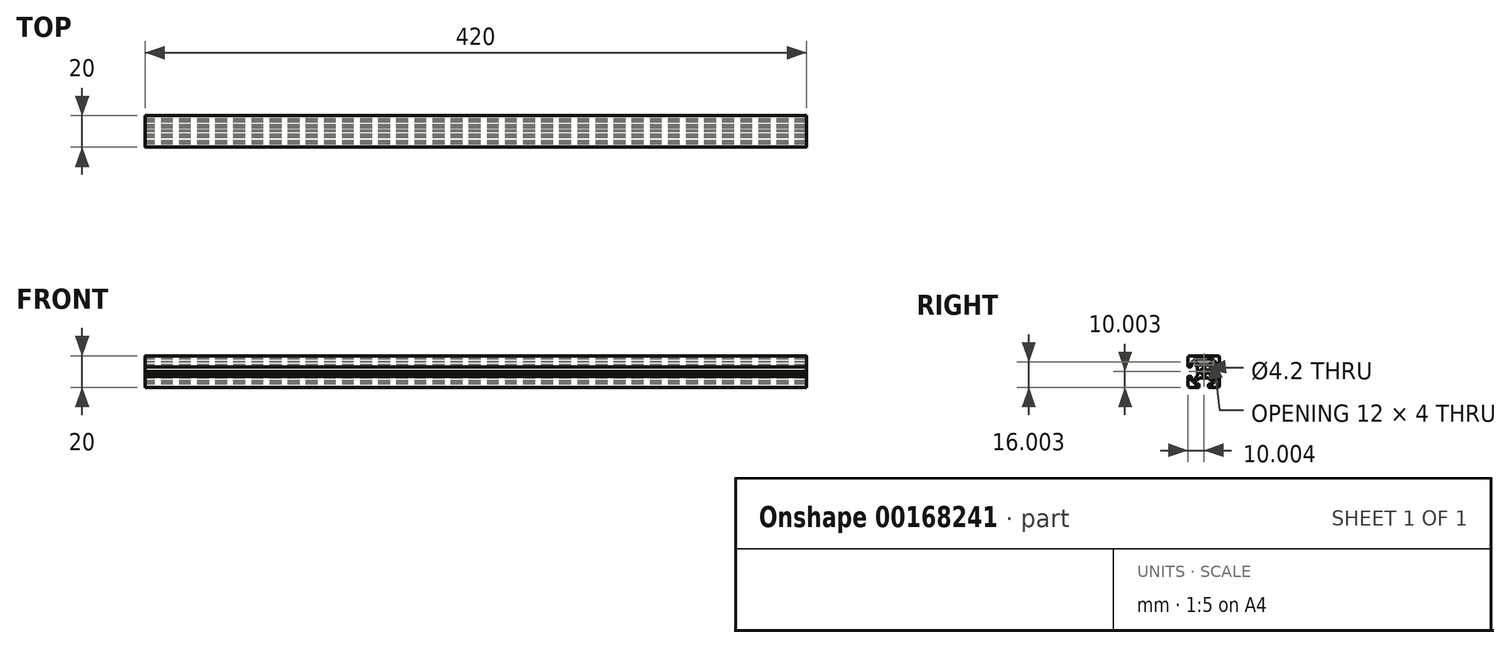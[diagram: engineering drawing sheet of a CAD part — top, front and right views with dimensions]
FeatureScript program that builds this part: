
annotation { "Feature Type Name" : "Feature", "Feature Type Description" : "" }
export const myFeature = defineFeature(function(context is Context, id is Id, definition is map)
    precondition{}
    {
        {
            var Q0;
            Q0=qCreatedBy(makeId("Right.planeOp"),FACE);
            var sketch = newSketch(context, id + "F0", { "sketchPlane" : qUnion([Q0])});
            skLineSegment(sketch, "E0", {"start": v(0.04, 10.07) * mm, "end": v(-8.96, 10.07) * mm});
            skLineSegment(sketch, "E1", {"start": v(-9.96, 9.07) * mm, "end": v(-9.96, 3.37) * mm});
            skLineSegment(sketch, "E2", {"start": v(-3.96, 3.01) * mm, "end": v(-3.96, 0.73) * mm});
            skLineSegment(sketch, "E3", {"start": v(0.04, 4.07) * mm, "end": v(-2.69, 4.07) * mm});
            skLineSegment(sketch, "E4", {"start": v(0.04, 8.07) * mm, "end": v(-5.46, 8.07) * mm});
            skLineSegment(sketch, "E5", {"start": v(-7.96, 6.07) * mm, "end": v(-7.96, 3.37) * mm});
            skLineSegment(sketch, "E6", {"start": v(-8.26, 3.07) * mm, "end": v(-9.66, 3.07) * mm});
            skLineSegment(sketch, "E7", {"start": v(-8.26, -2.93) * mm, "end": v(-9.66, -2.93) * mm});
            skLineSegment(sketch, "E8", {"start": v(-7.02, -5.93) * mm, "end": v(-7.96, -5.93) * mm});
            skLineSegment(sketch, "E9", {"start": v(-7.96, -3.23) * mm, "end": v(-7.96, -5.93) * mm});
            skLineSegment(sketch, "E10", {"start": v(-9.96, -3.23) * mm, "end": v(-9.96, -8.93) * mm});
            skLineSegment(sketch, "E11", {"start": v(-7.02, 6.07) * mm, "end": v(-7.96, 6.07) * mm});
            skLineSegment(sketch, "E12", {"start": v(-3.89, -0.33) * mm, "end": v(-3.66, 0.07) * mm});
            skLineSegment(sketch, "E13", {"start": v(-3.89, 0.48) * mm, "end": v(-3.66, 0.07) * mm});
            skLineSegment(sketch, "E14", {"start": v(-3.96, -2.43) * mm, "end": v(-3.96, -2.87) * mm});
            skLineSegment(sketch, "E15", {"start": v(-3.96, 3.01) * mm, "end": v(-7.02, 6.07) * mm});
            skLineSegment(sketch, "E16", {"start": v(-3.96, -2.87) * mm, "end": v(-7.02, -5.93) * mm});
            skLineSegment(sketch, "E17", {"start": v(-3.96, -2.43) * mm, "end": v(-3.7, -1.15) * mm});
            skArc(sketch, "E18", {"start": v(-3.89, -0.33) * mm, "mid": v(-3.96, -0.58) * mm, "end": v(-3.89, -0.83) * mm});
            skLineSegment(sketch, "E19", {"start": v(-3.89, -0.83) * mm, "end": v(-3.7, -1.15) * mm});
            skArc(sketch, "E20", {"start": v(-3.96, 0.73) * mm, "mid": v(-3.94, 0.6) * mm, "end": v(-3.89, 0.48) * mm});
            skArc(sketch, "E21", {"start": v(-8.26, 3.07) * mm, "mid": v(-8.04, 3.16) * mm, "end": v(-7.96, 3.37) * mm});
            skArc(sketch, "E22", {"start": v(-9.96, 3.37) * mm, "mid": v(-9.87, 3.16) * mm, "end": v(-9.66, 3.07) * mm});
            skArc(sketch, "E23", {"start": v(-7.96, -3.23) * mm, "mid": v(-8.04, -3.01) * mm, "end": v(-8.26, -2.93) * mm});
            skArc(sketch, "E24", {"start": v(-9.66, -2.93) * mm, "mid": v(-9.87, -3.01) * mm, "end": v(-9.96, -3.23) * mm});
            skLineSegment(sketch, "E25", {"start": v(-2.9, -3.93) * mm, "end": v(-0.61, -3.93) * mm});
            skArc(sketch, "E26", {"start": v(-3.26, -9.93) * mm, "mid": v(-3.04, -9.84) * mm, "end": v(-2.96, -9.63) * mm});
            skLineSegment(sketch, "E27", {"start": v(-5.96, -7.93) * mm, "end": v(-3.26, -7.93) * mm});
            skArc(sketch, "E28", {"start": v(-2.96, -8.23) * mm, "mid": v(-3.04, -8.01) * mm, "end": v(-3.26, -7.93) * mm});
            skLineSegment(sketch, "E29", {"start": v(-5.96, -6.99) * mm, "end": v(-5.96, -7.93) * mm});
            skLineSegment(sketch, "E30", {"start": v(-2.96, -8.23) * mm, "end": v(-2.96, -9.63) * mm});
            skLineSegment(sketch, "E31", {"start": v(-0.36, -3.86) * mm, "end": v(-0.06, -3.69) * mm});
            skArc(sketch, "E32", {"start": v(-0.61, -3.93) * mm, "mid": v(-0.48, -3.9) * mm, "end": v(-0.36, -3.86) * mm});
            skLineSegment(sketch, "E33", {"start": v(-2.9, -3.93) * mm, "end": v(-5.96, -6.99) * mm});
            skLineSegment(sketch, "E34", {"start": v(-3.26, -9.93) * mm, "end": v(-8.96, -9.93) * mm});
            skLineSegment(sketch, "E35", {"start": v(-3.04, 4.22) * mm, "end": v(-5.8, 6.99) * mm});
            skLineSegment(sketch, "E36", {"start": v(-5.96, 7.57) * mm, "end": v(-5.96, 7.34) * mm});
            skArc(sketch, "E37", {"start": v(0.04, -2.03) * mm, "mid": v(-2.06, 0.07) * mm, "end": v(0.04, 2.17) * mm});
            skArc(sketch, "E38", {"start": v(-9.96, -8.93) * mm, "mid": v(-9.66, -9.63) * mm, "end": v(-8.96, -9.93) * mm});
            skArc(sketch, "E39", {"start": v(-8.96, 10.07) * mm, "mid": v(-9.66, 9.78) * mm, "end": v(-9.96, 9.07) * mm});
            skArc(sketch, "E40", {"start": v(-5.46, 8.07) * mm, "mid": v(-5.8, 7.93) * mm, "end": v(-5.96, 7.57) * mm});
            skArc(sketch, "E41", {"start": v(-5.96, 7.34) * mm, "mid": v(-5.92, 7.15) * mm, "end": v(-5.8, 6.99) * mm});
            skArc(sketch, "E42", {"start": v(-3.04, 4.22) * mm, "mid": v(-2.88, 4.11) * mm, "end": v(-2.69, 4.07) * mm});
            skArc(sketch, "E43.MirrorCS", {"start": v(8.34, 3.07) * mm, "mid": v(8.13, 3.16) * mm, "end": v(8.04, 3.37) * mm});
            skArc(sketch, "E44.MirrorCS", {"start": v(5.54, 8.07) * mm, "mid": v(5.9, 7.93) * mm, "end": v(6.04, 7.57) * mm});
            skLineSegment(sketch, "E45.MirrorCS", {"start": v(3.98, -0.33) * mm, "end": v(3.74, 0.07) * mm});
            skArc(sketch, "E46.MirrorCS", {"start": v(3.04, -8.23) * mm, "mid": v(3.13, -8.01) * mm, "end": v(3.34, -7.93) * mm});
            skLineSegment(sketch, "E47.MirrorCS", {"start": v(3.98, -0.83) * mm, "end": v(3.8, -1.15) * mm});
            skArc(sketch, "E48.MirrorCS", {"start": v(3.34, -9.93) * mm, "mid": v(3.13, -9.84) * mm, "end": v(3.04, -9.63) * mm});
            skLineSegment(sketch, "E49.MirrorCS", {"start": v(7.1, -5.93) * mm, "end": v(8.04, -5.93) * mm});
            skArc(sketch, "E50.MirrorCS", {"start": v(3.98, -0.33) * mm, "mid": v(4.04, -0.58) * mm, "end": v(3.98, -0.83) * mm});
            skLineSegment(sketch, "E51.MirrorCS", {"start": v(4.04, -2.43) * mm, "end": v(3.8, -1.15) * mm});
            skArc(sketch, "E52.MirrorCS", {"start": v(9.74, -2.93) * mm, "mid": v(9.96, -3.01) * mm, "end": v(10.04, -3.23) * mm});
            skArc(sketch, "E53.MirrorCS", {"start": v(0.7, -3.93) * mm, "mid": v(0.63, -3.92) * mm, "end": v(0.57, -3.91) * mm});
            skLineSegment(sketch, "E54.MirrorCS", {"start": v(6.04, 7.57) * mm, "end": v(6.04, 7.34) * mm});
            skLineSegment(sketch, "E55.MirrorCS", {"start": v(6.04, -6.99) * mm, "end": v(6.04, -7.93) * mm});
            skArc(sketch, "E56.MirrorCS", {"start": v(6.04, 7.34) * mm, "mid": v(6, 7.15) * mm, "end": v(5.9, 6.99) * mm});
            skArc(sketch, "E57.MirrorCS", {"start": v(4.04, 0.73) * mm, "mid": v(4.03, 0.6) * mm, "end": v(3.98, 0.48) * mm});
            skArc(sketch, "E58.MirrorCS", {"start": v(8.04, -3.23) * mm, "mid": v(8.13, -3.01) * mm, "end": v(8.34, -2.93) * mm});
            skArc(sketch, "E59.MirrorCS", {"start": v(10.04, 3.37) * mm, "mid": v(9.96, 3.16) * mm, "end": v(9.74, 3.07) * mm});
            skArc(sketch, "E60.MirrorCS", {"start": v(3.13, 4.22) * mm, "mid": v(2.97, 4.11) * mm, "end": v(2.78, 4.07) * mm});
            skLineSegment(sketch, "E61.MirrorCS", {"start": v(7.1, 6.07) * mm, "end": v(8.04, 6.07) * mm});
            skLineSegment(sketch, "E62.MirrorCS", {"start": v(4.04, -2.43) * mm, "end": v(4.04, -2.87) * mm});
            skLineSegment(sketch, "E63.MirrorCS", {"start": v(3.98, 0.48) * mm, "end": v(3.74, 0.07) * mm});
            skLineSegment(sketch, "E64.MirrorCS", {"start": v(3.04, -8.23) * mm, "end": v(3.04, -9.63) * mm});
            skLineSegment(sketch, "E65.MirrorCS", {"start": v(3.13, 4.22) * mm, "end": v(5.9, 6.99) * mm});
            skLineSegment(sketch, "E66.MirrorCS", {"start": v(10.04, -3.23) * mm, "end": v(10.04, -8.93) * mm});
            skLineSegment(sketch, "E67.MirrorCS", {"start": v(8.04, -3.23) * mm, "end": v(8.04, -5.93) * mm});
            skLineSegment(sketch, "E68.MirrorCS", {"start": v(8.34, -2.93) * mm, "end": v(9.74, -2.93) * mm});
            skLineSegment(sketch, "E69.MirrorCS", {"start": v(8.34, 3.07) * mm, "end": v(9.74, 3.07) * mm});
            skLineSegment(sketch, "E70.MirrorCS", {"start": v(2.98, -3.93) * mm, "end": v(0.7, -3.93) * mm});
            skLineSegment(sketch, "E71.MirrorCS", {"start": v(4.04, 3.01) * mm, "end": v(4.04, 0.73) * mm});
            skLineSegment(sketch, "E72.MirrorCS", {"start": v(4.04, -2.87) * mm, "end": v(7.1, -5.93) * mm});
            skLineSegment(sketch, "E73.MirrorCS", {"start": v(2.98, -3.93) * mm, "end": v(6.04, -6.99) * mm});
            skArc(sketch, "E74.MirrorCS", {"start": v(9.04, 10.07) * mm, "mid": v(9.75, 9.78) * mm, "end": v(10.04, 9.07) * mm});
            skLineSegment(sketch, "E75.MirrorCS", {"start": v(6.04, -7.93) * mm, "end": v(3.34, -7.93) * mm});
            skLineSegment(sketch, "E76.MirrorCS", {"start": v(4.04, 3.01) * mm, "end": v(7.1, 6.07) * mm});
            skArc(sketch, "E77.MirrorCS", {"start": v(10.04, -8.93) * mm, "mid": v(9.75, -9.63) * mm, "end": v(9.04, -9.93) * mm});
            skLineSegment(sketch, "E78.MirrorCS", {"start": v(3.34, -9.93) * mm, "end": v(9.04, -9.93) * mm});
            skLineSegment(sketch, "E79.MirrorCS", {"start": v(8.04, 6.07) * mm, "end": v(8.04, 3.37) * mm});
            skLineSegment(sketch, "E80.MirrorCS", {"start": v(10.04, 9.07) * mm, "end": v(10.04, 3.37) * mm});
            skLineSegment(sketch, "E81.MirrorCS", {"start": v(0.04, 10.07) * mm, "end": v(9.04, 10.07) * mm});
            skLineSegment(sketch, "E82.MirrorCS", {"start": v(0.04, 8.07) * mm, "end": v(5.54, 8.07) * mm});
            skLineSegment(sketch, "E83.MirrorCS", {"start": v(0.04, 4.07) * mm, "end": v(2.78, 4.07) * mm});
            skArc(sketch, "E84.MirrorCS", {"start": v(0.04, -2.03) * mm, "mid": v(2.14, 0.07) * mm, "end": v(0.04, 2.17) * mm});
            skLineSegment(sketch, "E85", {"start": v(0.22, -3.85) * mm, "end": v(-0.06, -3.69) * mm});
            skArc(sketch, "E86", {"start": v(0.22, -3.85) * mm, "mid": v(0.4, -3.92) * mm, "end": v(0.57, -3.91) * mm});
            skSolve(sketch);
        }
        {
            var Q0;
            Q0=qSketchRegion(id+"F0",true);
            extrude(context, id + "F1", {"entities" : qUnion([Q0]), "endBound" : BoundingType.SYMMETRIC, "depth" : 420 * mm});
        }
    });
